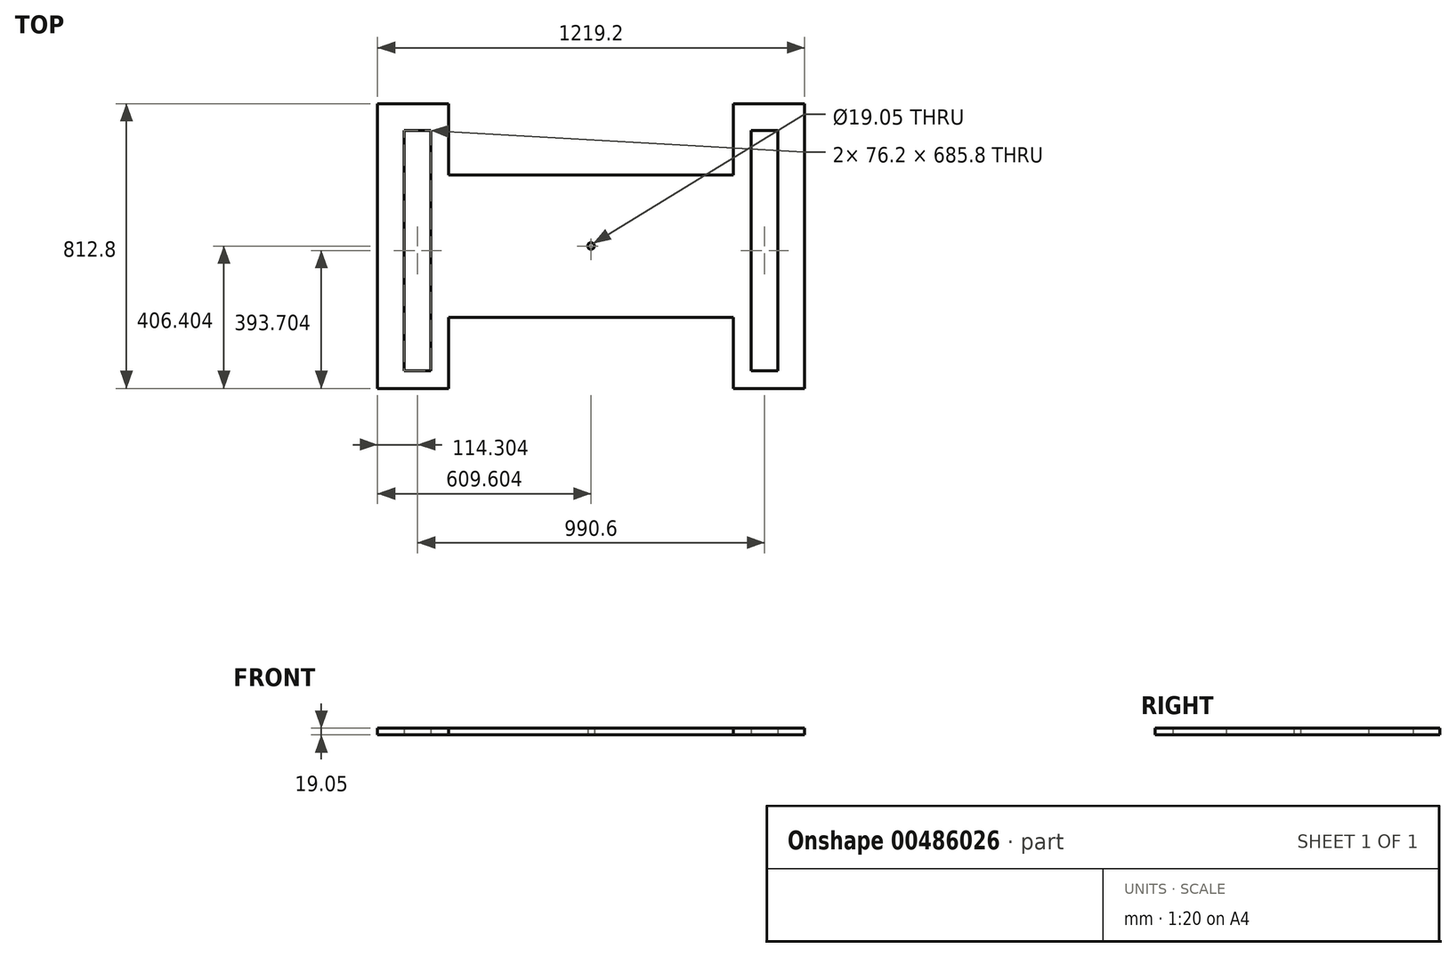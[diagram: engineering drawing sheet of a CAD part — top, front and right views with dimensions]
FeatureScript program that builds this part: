
annotation { "Feature Type Name" : "Feature", "Feature Type Description" : "" }
export const myFeature = defineFeature(function(context is Context, id is Id, definition is map)
    precondition{}
    {
        {
            var Q0;
            Q0=qCreatedBy(makeId("Top.planeOp"),FACE);
            var sketch = newSketch(context, id + "F0", { "sketchPlane" : qUnion([Q0])});
            skLineSegment(sketch, "E0", {"start": v(-136.62, -22.19) * mm, "end": v(66.58, -22.19) * mm});
            skLineSegment(sketch, "E1", {"start": v(66.58, -22.19) * mm, "end": v(66.58, 181.01) * mm});
            skLineSegment(sketch, "E2", {"start": v(-136.62, -22.19) * mm, "end": v(-136.62, 790.61) * mm});
            skLineSegment(sketch, "E3", {"start": v(-136.62, 790.61) * mm, "end": v(66.58, 790.61) * mm});
            skLineSegment(sketch, "E4", {"start": v(66.58, 790.61) * mm, "end": v(66.58, 587.41) * mm});
            skLineSegment(sketch, "E5", {"start": v(66.58, 587.41) * mm, "end": v(472.98, 587.41) * mm});
            skLineSegment(sketch, "E6", {"start": v(66.58, 181.01) * mm, "end": v(472.98, 181.01) * mm});
            skLineSegment(sketch, "E7", {"start": v(15.78, 28.61) * mm, "end": v(-60.42, 28.61) * mm});
            skLineSegment(sketch, "E8", {"start": v(-60.42, 28.61) * mm, "end": v(-60.42, 714.41) * mm});
            skLineSegment(sketch, "E9", {"start": v(-60.42, 714.41) * mm, "end": v(15.78, 714.41) * mm});
            skLineSegment(sketch, "E10", {"start": v(15.78, 714.41) * mm, "end": v(15.78, 28.61) * mm});
            skLineSegment(sketch, "E11.MirrorCS", {"start": v(1082.58, -22.19) * mm, "end": v(879.38, -22.19) * mm});
            skLineSegment(sketch, "E12.MirrorCS", {"start": v(879.38, -22.19) * mm, "end": v(879.38, 181.01) * mm});
            skLineSegment(sketch, "E13.MirrorCS", {"start": v(930.18, 714.41) * mm, "end": v(930.18, 28.61) * mm});
            skLineSegment(sketch, "E14.MirrorCS", {"start": v(1006.38, 714.41) * mm, "end": v(930.18, 714.41) * mm});
            skLineSegment(sketch, "E15.MirrorCS", {"start": v(1082.58, -22.19) * mm, "end": v(1082.58, 790.61) * mm});
            skLineSegment(sketch, "E16.MirrorCS", {"start": v(879.38, 587.41) * mm, "end": v(472.98, 587.41) * mm});
            skLineSegment(sketch, "E17.MirrorCS", {"start": v(879.38, 790.61) * mm, "end": v(879.38, 587.41) * mm});
            skLineSegment(sketch, "E18.MirrorCS", {"start": v(930.18, 28.61) * mm, "end": v(1006.38, 28.61) * mm});
            skLineSegment(sketch, "E19.MirrorCS", {"start": v(1006.38, 28.61) * mm, "end": v(1006.38, 714.41) * mm});
            skLineSegment(sketch, "E20.MirrorCS", {"start": v(1082.58, 790.61) * mm, "end": v(879.38, 790.61) * mm});
            skLineSegment(sketch, "E21.MirrorCS", {"start": v(879.38, 181.01) * mm, "end": v(472.98, 181.01) * mm});
            skCircle(sketch, "E22", {"center": v(472.98, 384.21) * mm, "radius": 9.52 * mm});
            skSolve(sketch);
        }
        {
            var Q0;
            Q0 = qSketchRegion(id + "F0", true);
            extrude(context, id + "F1", {"entities" : qUnion([Q0]), "depth" : 19.05 * mm});
        }
    });
